SOLIDWORKS PART (.sldprt)
format: sldprt  version: not decoded by parser v0  size: 589,824 bytes
history: native  units: mm
features: sketch x12, cut_extrude x6, extrude x5, fillet x4, plane x3, mirror x2, material x1, chamfer x1 (+8 scaffold rows collapsed)
feature tree (42):
  scaffold x8  (default folders/planes/origin — collapsed)
  material  "Duranickel(R) 301"
  plane  "Alzado"
  plane  "Planta"
  plane  "Vista lateral"
  sketch  "Croquis1"  dims[D1=5.0mm D2=2.5mm D3=42.8mm D4=21.4mm]
  extrude  "Extruir1"  Depth=36.4mm
  sketch  "Croquis2"  dims[c1.D1=0.9mm c1.D2=0.9mm c1.D3=1.0mm c1.D4=3.2mm c2.D1=1.5mm c2.D2=0.75mm]
  cut_extrude  "Cortar-Extruir1"  Depth=26mm
  sketch  "Croquis3"  dims[D1=12.0mm D2=3.3mm]
  cut_extrude  "Cortar-Extruir2"  Depth=2mm
  sketch  "Croquis4"  dims[D1=33.0mm D2=16.5mm]
  sketch  "Croquis6"  dims[D1=0.5mm D2=0.625mm]
  cut_extrude  "Cortar-Extruir3"  Depth=10mm
  fillet  "Redondeo1"  Radius=0.4mm
  fillet  "Redondeo2"  Radius=0.3mm
  chamfer  "Chaflán1"  Distance=0.25mm Angle=45deg
  sketch  "Croquis7"  dims[D1=0.9mm D2=20.6mm D3=41.2mm]
  extrude  "Extruir2"  Depth=0.6mm
  sketch  "Croquis8"  dims[D5=1.0mm D1=16.5mm D2=1.6mm D3=0.6mm D4=2.4mm]
  cut_extrude  "Cortar-Extruir4"  Depth=0.5mm
  mirror  "Simetría1"
  sketch  "Croquis9"  dims[D1=0.0mm]
  extrude  "Extruir3"  Depth=0.5mm
  fillet  "Redondeo3"  Radius=0.2mm
  sketch  "Croquis10"  dims[D1=0.0mm]
  extrude  "Extruir4"  Depth=0.5mm
  fillet  "Redondeo4"  Radius=0.2mm
  sketch  "Croquis11"
  cut_extrude  "Línea de partición2"  [1 undecoded]
  sketch  "Croquis12"
  cut_extrude  "Línea de partición3"  [1 undecoded]
  sketch  "Croquis13"  dims[D5=1.5mm D1=36.0mm D2=18.0mm D3=3.5mm D4=3.5mm]
  extrude  "Extruir5"  Depth=0.05mm
  mirror  "Simetría2"
decode coverage: 24 of 30 modeling features carry decoded parameters
note: 2 parameter values undecoded
note: suppression state not decoded; provenance and decode notes live in map.json
